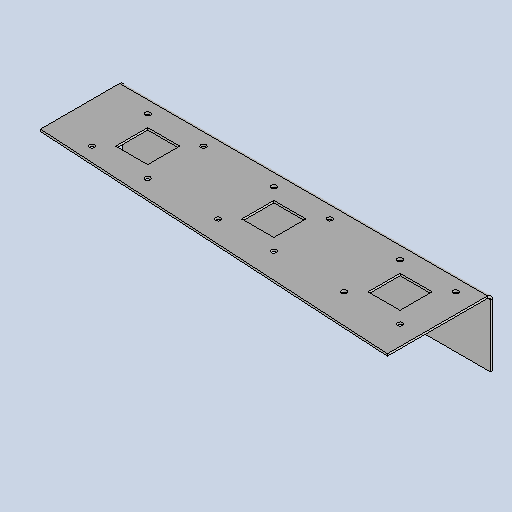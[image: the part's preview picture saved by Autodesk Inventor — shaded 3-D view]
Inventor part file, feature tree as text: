
AUTODESK INVENTOR PART (.ipt)
format: ipt  version: 2025.3 (Build 293356030, 356C)  size: 238,592 bytes
history: native  units: mm
features: sheet_metal_op x4, other x4, sketch x3, pattern_linear x1
ambient origin geometry x8: Origin, YZ Plane, XZ Plane, XY Plane, X Axis, Y Axis, Z Axis, Center Point
bodies: Solid1 (feature_tree)
feature tree (12):
  sheet_metal_op  "Face1"
  pattern_linear  "Rectangular Pattern1"  Count1=10  [1 undecoded]
  sheet_metal_op  "Flange3"
  sketch  "Sketch1"  dims[d2=2.0mm d32=100.0mm]
  other  "Plate1"
  sketch  "Sketch8"  dims[d51=30.5mm]
  sketch  "Sketch9"  dims[d52=30.5mm d53=5.0mm d55=2.0mm d56=0.0mm d57=30.0mm d59=120.0mm d60=80.0mm d61=350.0mm d62=2.0mm d63=1.0mm d64=4.0mm d65=2.75mm d66=64.0mm d67=90.0deg d68=2.75mm d69=8.0mm d70=2.0mm d71=2.75mm d72=45.0mm d73=43.0mm d74=15.933243mm d75=75.0mm]
  other  "Plate4"
  sheet_metal_op  "Bend3"
  sheet_metal_op  "Corner3"
  other  "Cut3"
  other  "Definition1"
note: 1 required parameter value undecoded (feature->parameter linkage not recoverable at this tier; creation-order binding heuristic only, values carry confidence <= 0.55)
